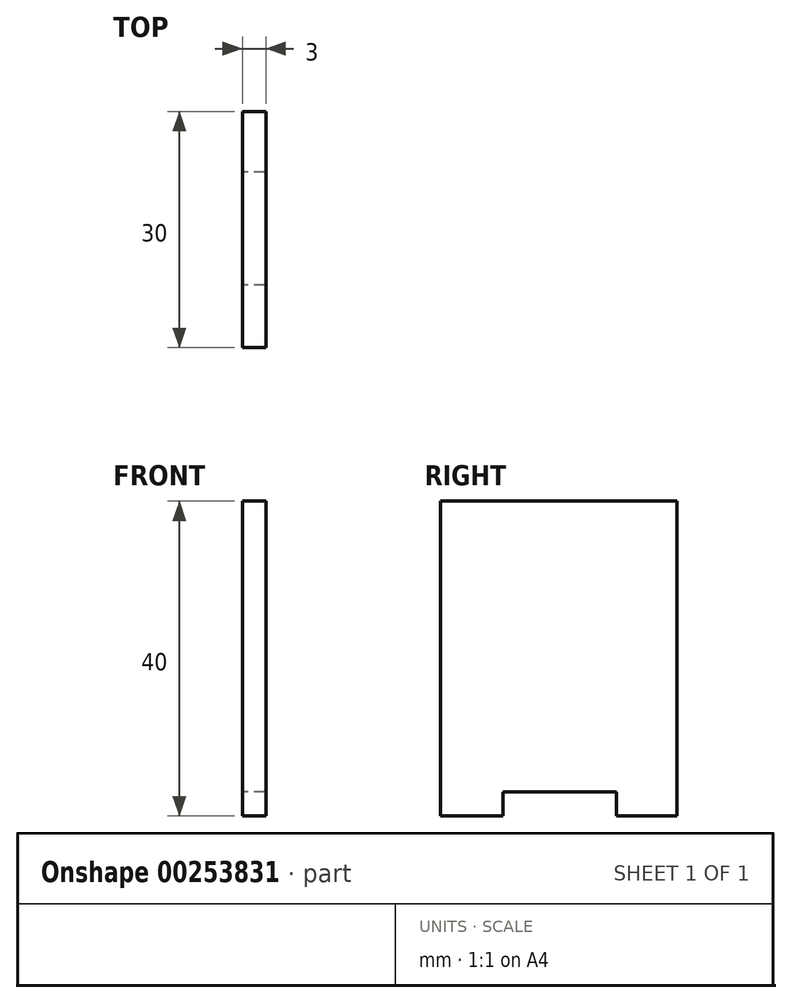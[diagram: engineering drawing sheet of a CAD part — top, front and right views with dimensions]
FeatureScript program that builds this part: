
annotation { "Feature Type Name" : "Feature", "Feature Type Description" : "" }
export const myFeature = defineFeature(function(context is Context, id is Id, definition is map)
    precondition{}
    {
        {
            var Q0;
            Q0=qCreatedBy(makeId("Right.planeOp"),FACE);
            var sketch = newSketch(context, id + "F0", { "sketchPlane" : qUnion([Q0])});
            skLineSegment(sketch, "E0", {"start": v(-15, 20) * mm, "end": v(-15, -20) * mm});
            skLineSegment(sketch, "E1", {"start": v(-15, -20) * mm, "end": v(-7.06, -20) * mm});
            skLineSegment(sketch, "E2", {"start": v(-7.06, -20) * mm, "end": v(-7.06, -16.95) * mm});
            skLineSegment(sketch, "E3", {"start": v(-7.06, -16.95) * mm, "end": v(7.31, -16.95) * mm});
            skLineSegment(sketch, "E4", {"start": v(7.31, -16.95) * mm, "end": v(7.31, -20) * mm});
            skLineSegment(sketch, "E5", {"start": v(7.31, -20) * mm, "end": v(15, -20) * mm});
            skLineSegment(sketch, "E6", {"start": v(15, -20) * mm, "end": v(15, 20) * mm});
            skLineSegment(sketch, "E7", {"start": v(15, 20) * mm, "end": v(-15, 20) * mm});
            skSolve(sketch);
        }
        {
            var Q0;
            Q0 = qSketchRegion(id + "F0", true);
            extrude(context, id + "F1", {"entities" : qUnion([Q0]), "depth" : 3 * mm});
        }
    });
